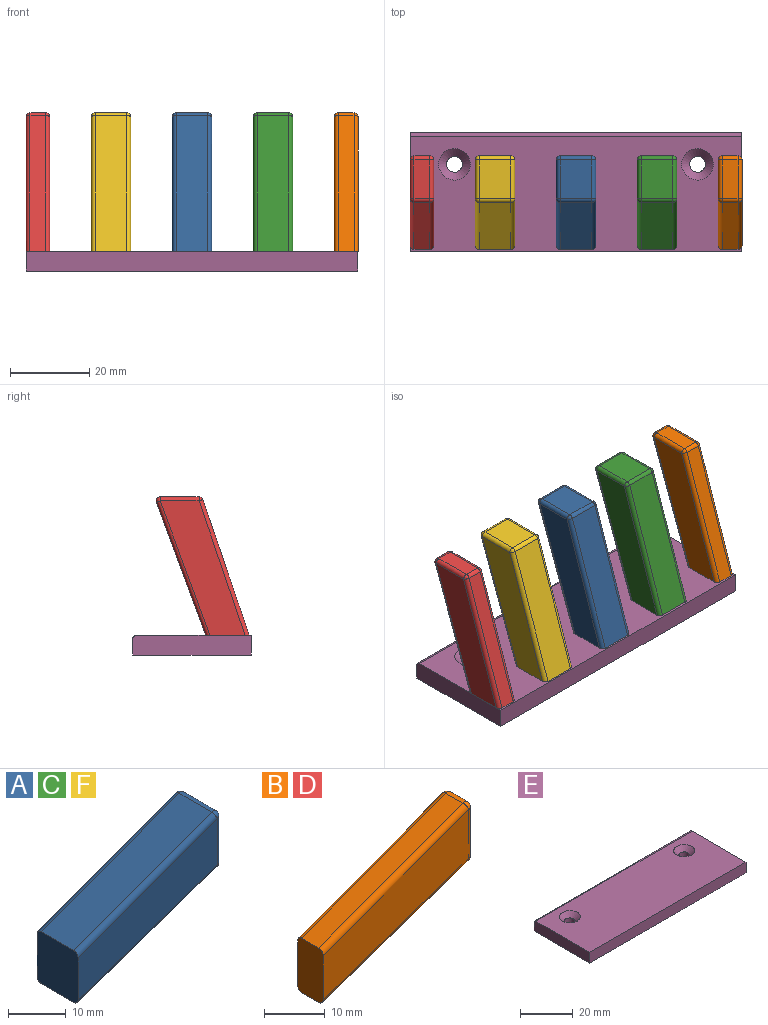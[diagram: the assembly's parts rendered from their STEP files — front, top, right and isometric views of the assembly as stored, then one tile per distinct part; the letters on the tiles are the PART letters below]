
ASSEMBLY  parts=6 mates=5
PART A: 18 faces, bbox 35.3x10x23.6 mm
  f0: plane 33.65x12.5mm, normal (-0.35,0,0.94), area 287.2mm2, adj f1,f6,f7,f8
  f1: plane 11x10mm, normal (-1,0,0), area 109.1mm2, adj f0,f2,f4,f5,f6,f8,f11,f14
  f2: plane 34.32x11.77mm, normal (0.32,0,-0.95), area 290.3mm2, adj f1,f11,f14,f17
  f3: plane 9.85x8mm, normal (1,0,0), area 78.8mm2, adj f7,f12,f13,f17
  f4: plane 34x21.5mm, normal (0,-1,0), area 318.3mm2, adj f1,f6,f11,f12
  f5: plane 34x21.5mm, normal (0,1,0), area 318.3mm2, adj f1,f8,f13,f14
  f6: cylinder r=1mm len=34.35mm, axis (0.94,0,0.35), area 56.6mm2, adj f0,f1,f4,f9
  f7: cylinder r=1mm len=8mm, axis (0,1,0), area 15.4mm2, adj f0,f3,f9,f10
  f8: cylinder r=1mm len=34.35mm, axis (-0.94,0,-0.35), area 56.6mm2, adj f0,f1,f5,f10
  f9: sphere r=1mm, area 1.9mm2, adj f6,f7,f12
  f10: sphere r=1mm, area 1.9mm2, adj f7,f8,f13
  f11: cylinder r=1mm len=34.65mm, axis (-0.95,0,-0.32), area 56.8mm2, adj f1,f2,f4,f15
  f12: cylinder r=1mm len=9.85mm, axis (0,0,-1), area 15.5mm2, adj f3,f4,f9,f15
  f13: cylinder r=1mm len=9.85mm, axis (0,0,1), area 15.5mm2, adj f3,f5,f10,f16
  f14: cylinder r=1mm len=34.65mm, axis (0.95,0,0.32), area 56.8mm2, adj f1,f2,f5,f16
  f15: sphere r=1mm, area 1.2mm2, adj f11,f12,f17
  f16: sphere r=1mm, area 1.2mm2, adj f13,f14,f17
  f17: cylinder r=1mm len=8mm, axis (0,-1,0), area 9.9mm2, adj f2,f3,f15,f16
PART B: 18 faces, bbox 35.3x6x23.6 mm
  f0: plane 33.65x12.5mm, normal (-0.35,0,0.94), area 143.6mm2, adj f1,f6,f7,f8
  f1: plane 11x6mm, normal (-1,0,0), area 65.1mm2, adj f0,f2,f4,f5,f6,f8,f11,f14
  f2: plane 34.32x11.77mm, normal (0.32,0,-0.95), area 145.1mm2, adj f1,f11,f14,f17
  f3: plane 9.85x4mm, normal (1,0,0), area 39.4mm2, adj f7,f12,f13,f17
  f4: plane 34x21.5mm, normal (0,-1,0), area 318.3mm2, adj f1,f6,f11,f12
  f5: plane 34x21.5mm, normal (0,1,0), area 318.3mm2, adj f1,f8,f13,f14
  f6: cylinder r=1mm len=34.35mm, axis (0.94,0,0.35), area 56.6mm2, adj f0,f1,f4,f9
  f7: cylinder r=1mm len=4mm, axis (0,1,0), area 7.7mm2, adj f0,f3,f9,f10
  f8: cylinder r=1mm len=34.35mm, axis (-0.94,0,-0.35), area 56.6mm2, adj f0,f1,f5,f10
  f9: sphere r=1mm, area 1.9mm2, adj f6,f7,f12
  f10: sphere r=1mm, area 1.9mm2, adj f7,f8,f13
  f11: cylinder r=1mm len=34.65mm, axis (-0.95,0,-0.32), area 56.8mm2, adj f1,f2,f4,f15
  f12: cylinder r=1mm len=9.85mm, axis (0,0,-1), area 15.5mm2, adj f3,f4,f9,f15
  f13: cylinder r=1mm len=9.85mm, axis (0,0,1), area 15.5mm2, adj f3,f5,f10,f16
  f14: cylinder r=1mm len=34.65mm, axis (0.95,0,0.32), area 56.8mm2, adj f1,f2,f5,f16
  f15: sphere r=1mm, area 1.2mm2, adj f11,f12,f17
  f16: sphere r=1mm, area 1.2mm2, adj f13,f14,f17
  f17: cylinder r=1mm len=4mm, axis (0,-1,0), area 5mm2, adj f2,f3,f15,f16
PART C: same geometry as A
PART D: same geometry as B
PART E: 11 faces, bbox 84x30x5 mm
  f0: plane 30x5mm, normal (1,0,0), area 149.8mm2, adj f1,f4,f6,f7,f8
  f1: plane 84x4mm, normal (0,1,0), area 336mm2, adj f0,f2,f6,f8
  f2: plane 30x5mm, normal (-1,0,0), area 149.8mm2, adj f1,f4,f6,f7,f8
  f3: cylinder r=2mm len=4mm, axis (0,0,1), area 37.7mm2, adj f6,f9
  f4: plane 84x5mm, normal (0,-1,0), area 420mm2, adj f0,f2,f6,f7
  f5: cylinder r=2mm len=4mm, axis (0,0,1), area 37.7mm2, adj f6,f10
  f6: plane 84x30mm, normal (0,0,-1), area 2494.9mm2, adj f0,f1,f2,f3,f4,f5
  f7: plane 84x29mm, normal (0,0,1), area 2335.5mm2, adj f0,f2,f4,f8,f9,f10
  f8: cylinder r=1mm len=84mm, axis (-1,0,0), area 131.9mm2, adj f0,f1,f2,f7
  f9: cone r=2mm half-angle=45deg, axis (0,0,1), area 53.3mm2, adj f3,f7
  f10: cone r=2mm half-angle=45deg, axis (0,0,1), area 53.3mm2, adj f5,f7
PART F: same geometry as A
PLACE A rot(axis=(-0.58,-0.58,-0.58),120deg) t=(43.54,11.32,36.86)mm
PLACE B rot(axis=(-0.58,-0.58,-0.58),120deg) t=(80.54,11.32,36.86)mm
PLACE C rot(axis=(-0.58,-0.58,-0.58),120deg) t=(64.04,11.32,36.86)mm
PLACE D rot(axis=(-0.58,-0.58,-0.58),120deg) t=(2.54,11.32,36.86)mm
PLACE E t=(-3.46,6.82,1.86)mm
PLACE F rot(axis=(-0.58,-0.58,-0.58),120deg) t=(23.04,11.32,36.86)mm
MATE fastened F.f1 <-> E.f7  axis (0,0,-1) through (18.04,12.82,1.86)mm
MATE fastened A.f1 <-> E.f7  axis (0,0,-1) through (38.54,12.82,1.86)mm
MATE fastened C.f1 <-> E.f7  axis (0,0,-1) through (59.04,12.82,1.86)mm
MATE fastened B.f1 <-> E.f7  axis (0,0,-1) through (77.54,12.82,1.86)mm
MATE fastened D.f1 <-> E.f7  axis (0,0,-1) through (-0.46,12.82,1.86)mm
